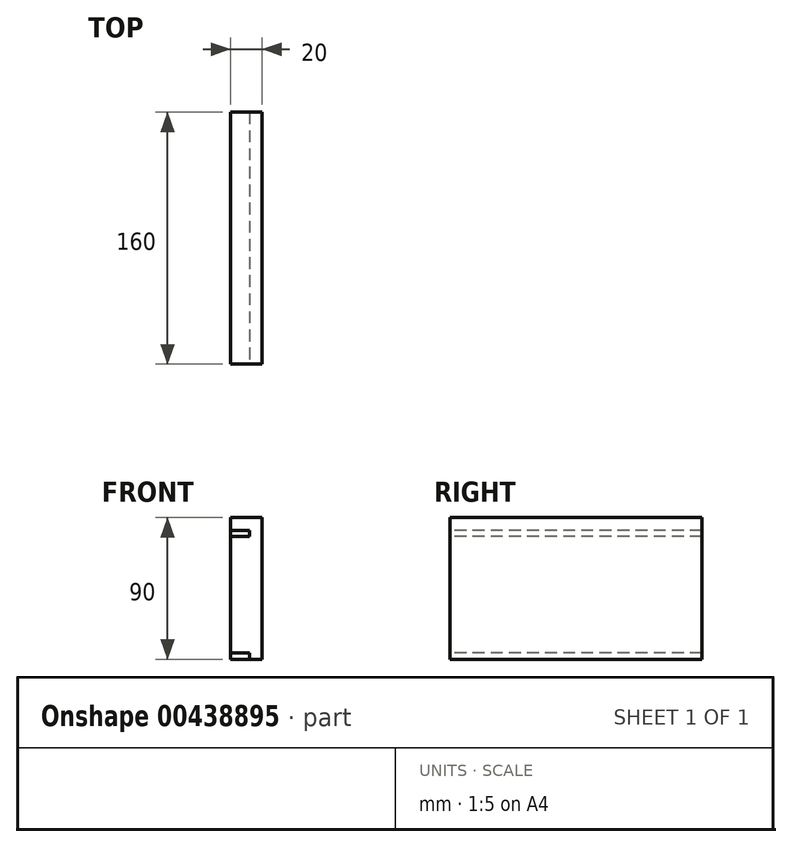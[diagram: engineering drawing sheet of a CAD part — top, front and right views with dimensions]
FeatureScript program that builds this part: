
annotation { "Feature Type Name" : "Feature", "Feature Type Description" : "" }
export const myFeature = defineFeature(function(context is Context, id is Id, definition is map)
    precondition{}
    {
        {
            var Q0;
            Q0=qCreatedBy(makeId("Right.planeOp"),FACE);
            var sketch = newSketch(context, id + "F0", { "sketchPlane" : qUnion([Q0])});
            skLineSegment(sketch, "E0", {"start": v(-65.75, 90) * mm, "end": v(-65.75, 0) * mm});
            skLineSegment(sketch, "E1", {"start": v(94.25, 90) * mm, "end": v(94.25, 0) * mm});
            skLineSegment(sketch, "E2", {"start": v(-65.75, 4) * mm, "end": v(-65.75, 0) * mm});
            skLineSegment(sketch, "E3", {"start": v(-65.75, 90) * mm, "end": v(94.25, 90) * mm});
            skLineSegment(sketch, "E4", {"start": v(-65.75, 0) * mm, "end": v(94.25, 0) * mm});
            skLineSegment(sketch, "E5", {"start": v(94.25, 4) * mm, "end": v(-65.75, 4) * mm});
            skLineSegment(sketch, "E6", {"start": v(94.25, 82) * mm, "end": v(-65.75, 82) * mm});
            skLineSegment(sketch, "E7", {"start": v(-65.75, 82) * mm, "end": v(-65.75, 90) * mm});
            skLineSegment(sketch, "E8", {"start": v(94.25, 82) * mm, "end": v(94.25, 78) * mm});
            skLineSegment(sketch, "E9", {"start": v(94.25, 78) * mm, "end": v(-65.75, 78) * mm});
            skLineSegment(sketch, "E10", {"start": v(-65.75, 78) * mm, "end": v(-65.75, 82) * mm});
            skSolve(sketch);
        }
        {
            var Q0;
            Q0=makeQuery(id+"F0.imprint","IMPRINT",FACE,{"disambiguationData":[TD([[makeQuery(id+"F0.imprint","IMPRINT",EDGE,{"derivedFrom":sQuery(id+"F0.wireOp",EDGE,"E0")}),1.0]])]});
            var Q1;
            {var subQ0=sQuery(id+"F0.wireOp",EDGE,"E3");Q1=makeQuery(id+"F0.imprint","IMPRINT",FACE,{"disambiguationData":[TD([[makeQuery(id+"F0.imprint","IMPRINT",EDGE,{"derivedFrom":subQ0}),-1.0]])]});}
            extrude(context, id + "F1", {"entities" : qUnion([Q0, Q1]), "depth" : 20 * mm});
        }
        {
            var Q0;
            Q0=makeQuery(id+"F0.imprint","IMPRINT",FACE,{"disambiguationData":[TD([[makeQuery(id+"F0.imprint","IMPRINT",EDGE,{"derivedFrom":sQuery(id+"F0.wireOp",EDGE,"E6")}),1.0]])]});
            var Q1;
            {var subQ0=sQuery(id+"F0.wireOp",EDGE,"E4");Q1=makeQuery(id+"F0.imprint","IMPRINT",FACE,{"disambiguationData":[TD([[makeQuery(id+"F0.imprint","IMPRINT",EDGE,{"derivedFrom":subQ0}),1.0]])]});}
            extrude(context, id + "F2", {"entities" : qUnion([Q0, Q1]), "depth" : 12 * mm});
        }
    });
